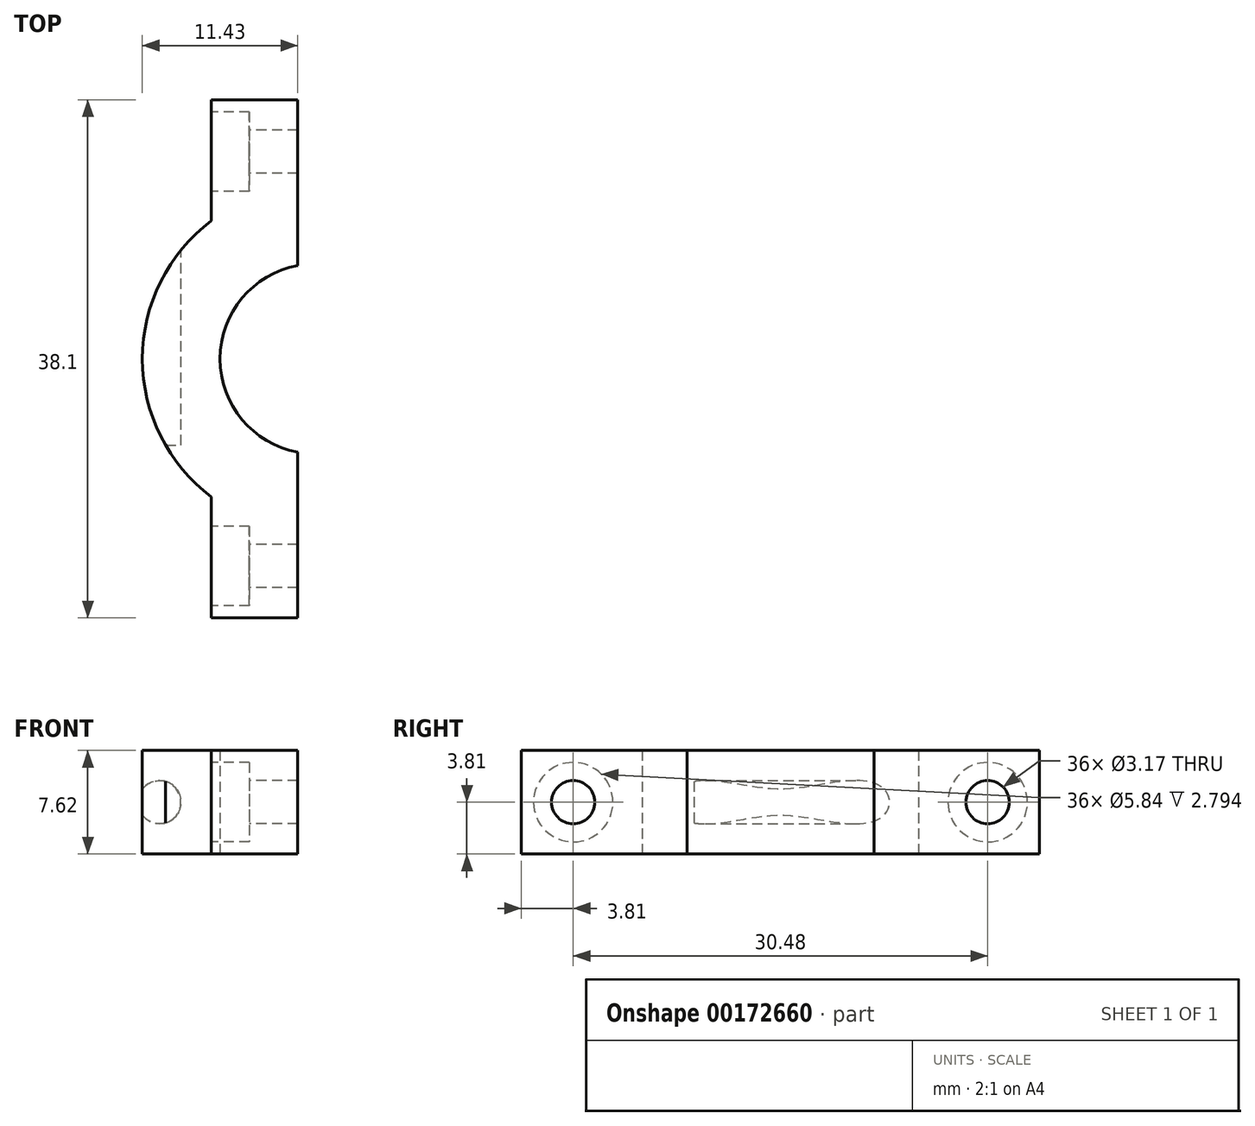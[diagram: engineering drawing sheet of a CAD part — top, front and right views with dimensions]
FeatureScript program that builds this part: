
annotation { "Feature Type Name" : "Feature", "Feature Type Description" : "" }
export const myFeature = defineFeature(function(context is Context, id is Id, definition is map)
    precondition{}
    {
        {
            var Q0;
            Q0=qCreatedBy(makeId("Top.planeOp"),FACE);
            var sketch = newSketch(context, id + "F0", { "sketchPlane" : qUnion([Q0])});
            skArc(sketch, "E0", {"start": v(12.64, 1.27) * mm, "mid": v(0, 12.7) * mm, "end": v(-12.64, 1.27) * mm});
            skArc(sketch, "E1", {"start": v(6.87, 1.27) * mm, "mid": v(0, 6.99) * mm, "end": v(-6.87, 1.27) * mm});
            skLineSegment(sketch, "E2", {"start": v(0, 6.99) * mm, "end": v(0, 12.7) * mm, "construction": true});
            skLineSegment(sketch, "E3", {"start": v(-19.05, 7.62) * mm, "end": v(-19.05, 1.27) * mm});
            skLineSegment(sketch, "E4", {"start": v(-19.05, 1.27) * mm, "end": v(-6.87, 1.27) * mm});
            skLineSegment(sketch, "E5", {"start": v(19.05, 1.27) * mm, "end": v(19.05, 7.62) * mm});
            skLineSegment(sketch, "E6", {"start": v(-19.05, 7.62) * mm, "end": v(19.05, 7.62) * mm});
            skLineSegment(sketch, "E7", {"start": v(-11.43, 7.62) * mm, "end": v(-11.43, 1.27) * mm});
            skLineSegment(sketch, "E8", {"start": v(11.43, 7.62) * mm, "end": v(11.43, 1.27) * mm});
            skPoint(sketch, "E9.orphan", {"position": v(19.05, 12.7) * mm});
            skLineSegment(sketch, "E10.trimOffspring", {"start": v(6.87, 1.27) * mm, "end": v(19.05, 1.27) * mm});
            skPoint(sketch, "E11.orphan", {"position": v(0, -12.7) * mm});
            skSolve(sketch);
        }
        {
            var Q0;
            Q0 = qSketchRegion(id + "F0", true);
            extrude(context, id + "F1", {"entities" : qUnion([Q0]), "depth" : 7.62 * mm});
        }
        {
            var Q0;
            {var subQ0=sQuery(id+"F0.wireOp",EDGE,"E6");var subQ1=makeQuery(id+"F0.imprint","INTERSECT",VERTEX,{"derivedFrom":[subQ0,sQuery(id+"F0.wireOp",EDGE,"E8")]});Q0=makeQuery(id+"F1.opExtrude","SWEPT_FACE",FACE,{"disambiguationData":[OSD([subQ0]),TDD([makeQuery(id+"F0.imprint","IMPRINT",EDGE,{"disambiguationData":[TD([[subQ1,1.0]])],"derivedFrom":subQ0}),makeQuery(id+"F0.imprint","IMPRINT",EDGE,{"disambiguationData":[TD([[makeQuery(id+"F0.imprint","INTERSECT",VERTEX,{"derivedFrom":[sQuery(id+"F0.wireOp",EDGE,"E5"),subQ0]}),1.0]])],"derivedFrom":subQ0})])]});}
            var sketch = newSketch(context, id + "F2", { "sketchPlane" : qUnion([Q0])});
            skCircle(sketch, "E12", {"center": v(-15.24, 3.81) * mm, "radius": 2.92 * mm});
            skPoint(sketch, "E12.centerSnap0", {"position": v(-10.16, 3.81) * mm});
            skCircle(sketch, "E13", {"center": v(-15.24, 3.81) * mm, "radius": 1.59 * mm});
            skSolve(sketch);
        }
        {
            var Q0;
            {var subQ0=sQuery(id+"F0.wireOp",EDGE,"E6");var subQ1=makeQuery(id+"F0.imprint","INTERSECT",VERTEX,{"derivedFrom":[subQ0,sQuery(id+"F0.wireOp",EDGE,"E7")]});Q0=makeQuery(id+"F1.opExtrude","SWEPT_FACE",FACE,{"disambiguationData":[OSD([subQ0]),TDD([makeQuery(id+"F0.imprint","IMPRINT",EDGE,{"disambiguationData":[TD([[makeQuery(id+"F0.imprint","INTERSECT",VERTEX,{"derivedFrom":[sQuery(id+"F0.wireOp",EDGE,"E3"),subQ0]}),-1.0]])],"derivedFrom":subQ0}),makeQuery(id+"F0.imprint","IMPRINT",EDGE,{"disambiguationData":[TD([[subQ1,-1.0]])],"derivedFrom":subQ0})])]});}
            var sketch = newSketch(context, id + "F3", { "sketchPlane" : qUnion([Q0])});
            skCircle(sketch, "E14", {"center": v(15.24, 3.81) * mm, "radius": 1.59 * mm});
            skPoint(sketch, "E14.centerSnap0", {"position": v(19.05, 3.81) * mm});
            skCircle(sketch, "E15", {"center": v(15.24, 3.81) * mm, "radius": 2.92 * mm});
            skSolve(sketch);
        }
        {
            var Q0;
            Q0=makeQuery(id+"F2.imprint","IMPRINT",FACE,{"disambiguationData":[TD([[makeQuery(id+"F2.imprint","IMPRINT",EDGE,{"derivedFrom":sQuery(id+"F2.wireOp",EDGE,"E13")}),1.0]])]});
            var Q1;
            Q1=makeQuery(id+"F3.imprint","IMPRINT",FACE,{"disambiguationData":[TD([[makeQuery(id+"F3.imprint","IMPRINT",EDGE,{"derivedFrom":sQuery(id+"F3.wireOp",EDGE,"E14")}),1.0]])]});
            extrude(context, id + "F4", {"entities" : qUnion([Q0, Q1]), "operationType" : NewBodyOperationType.REMOVE, "oppositeDirection" : true, "depth" : 25.4 * mm});
        }
        {
            var Q0;
            Q0=makeQuery(id+"F2.imprint","IMPRINT",FACE,{"disambiguationData":[TD([[makeQuery(id+"F2.imprint","IMPRINT",EDGE,{"derivedFrom":sQuery(id+"F2.wireOp",EDGE,"E12")}),1.0]])]});
            var Q1;
            Q1=makeQuery(id+"F3.imprint","IMPRINT",FACE,{"disambiguationData":[TD([[makeQuery(id+"F3.imprint","IMPRINT",EDGE,{"derivedFrom":sQuery(id+"F3.wireOp",EDGE,"E14")}),-1.0]])]});
            extrude(context, id + "F5", {"entities" : qUnion([Q0, Q1]), "operationType" : NewBodyOperationType.REMOVE, "oppositeDirection" : true, "depth" : 2.8 * mm});
        }
        {
            var Q0;
            Q0=makeQuery(id+"F1.opExtrude","SWEPT_BODY",BODY,{"disambiguationData":[OSD([sQuery(id+"F0.wireOp",EDGE,"E0"),sQuery(id+"F0.wireOp",EDGE,"E1"),sQuery(id+"F0.wireOp",EDGE,"E3"),sQuery(id+"F0.wireOp",EDGE,"E4"),sQuery(id+"F0.wireOp",EDGE,"E5"),sQuery(id+"F0.wireOp",EDGE,"E6"),sQuery(id+"F0.wireOp",EDGE,"E10.trimOffspring")])]});
            var Q1;
            Q1=qCreatedBy(makeId("Origin.pointOp"),VERTEX);
            var Q2;
            Q2=makeQuery(id+"F1.opExtrude","SWEPT_EDGE",EDGE,{"disambiguationData":[OSD([sQuery(id+"F0.wireOp",EDGE,"E5"),sQuery(id+"F0.wireOp",EDGE,"E6")])]});
            transform(context, id + "F6", {"entities" : qUnion([Q0]), "transformType" : TransformType.ROTATION, "transformAxis" : qUnion([Q2]), "angle" : 90 * degree, "oppositeDirection" : true, "makeCopy" : false});
        }
    });
